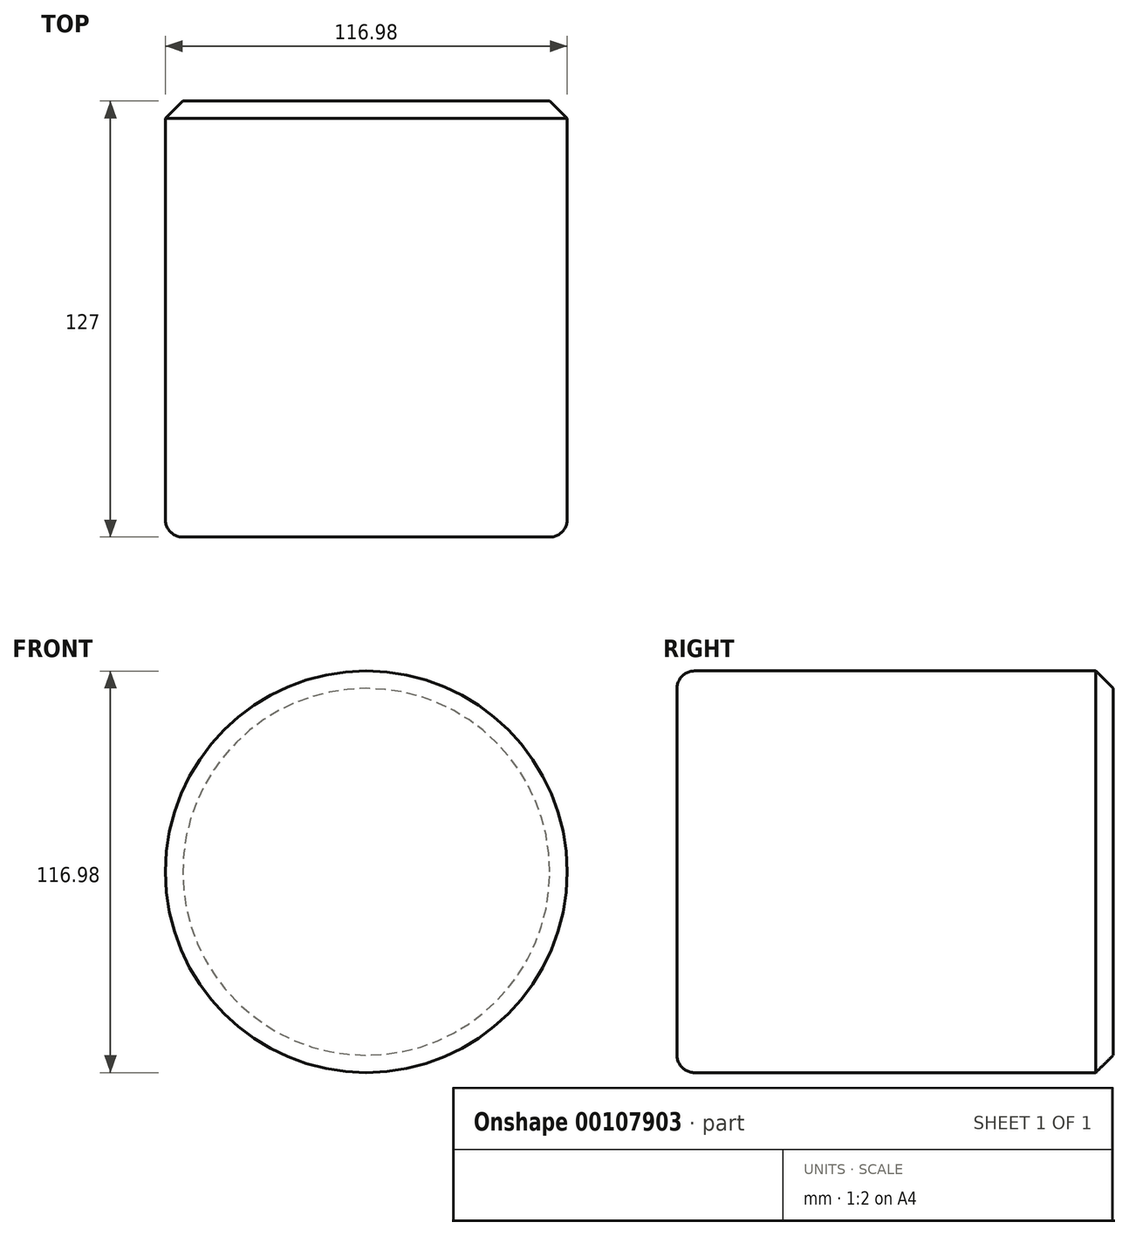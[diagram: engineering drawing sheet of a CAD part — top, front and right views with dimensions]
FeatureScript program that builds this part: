
annotation { "Feature Type Name" : "Feature", "Feature Type Description" : "" }
export const myFeature = defineFeature(function(context is Context, id is Id, definition is map)
    precondition{}
    {
        {
            var Q0;
            Q0=qCreatedBy(makeId("Front.planeOp"),FACE);
            var sketch = newSketch(context, id + "F0", { "sketchPlane" : qUnion([Q0])});
            skCircle(sketch, "E0", {"center": v(0, 0) * mm, "radius": 58.5 * mm});
            skSolve(sketch);
        }
        {
            var Q0;
            Q0 = qSketchRegion(id + "F0", true);
            extrude(context, id + "F1", {"entities" : qUnion([Q0]), "depth" : 127 * mm});
        }
        {
            var Q0;
            Q0=makeQuery(id+"F1.opExtrude","CAP_EDGE",EDGE,{"disambiguationData":[OSD([sQuery(id+"F0.wireOp",EDGE,"E0")])],"isStart":false});
            fillet(context, id + "F2", {"entities" : qUnion([Q0]), "radius" : 5.08 * mm, "tangentPropagation" : true, "allowEdgeOverflow" : false});
        }
        {
            var Q0;
            Q0=makeQuery(id+"F1.opExtrude","CAP_EDGE",EDGE,{"disambiguationData":[OSD([sQuery(id+"F0.wireOp",EDGE,"E0")])],"isStart":true});
            chamfer(context, id + "F3", {"entities" : qUnion([Q0]), "width" : 5.08 * mm, "tangentPropagation" : true});
        }
    });
